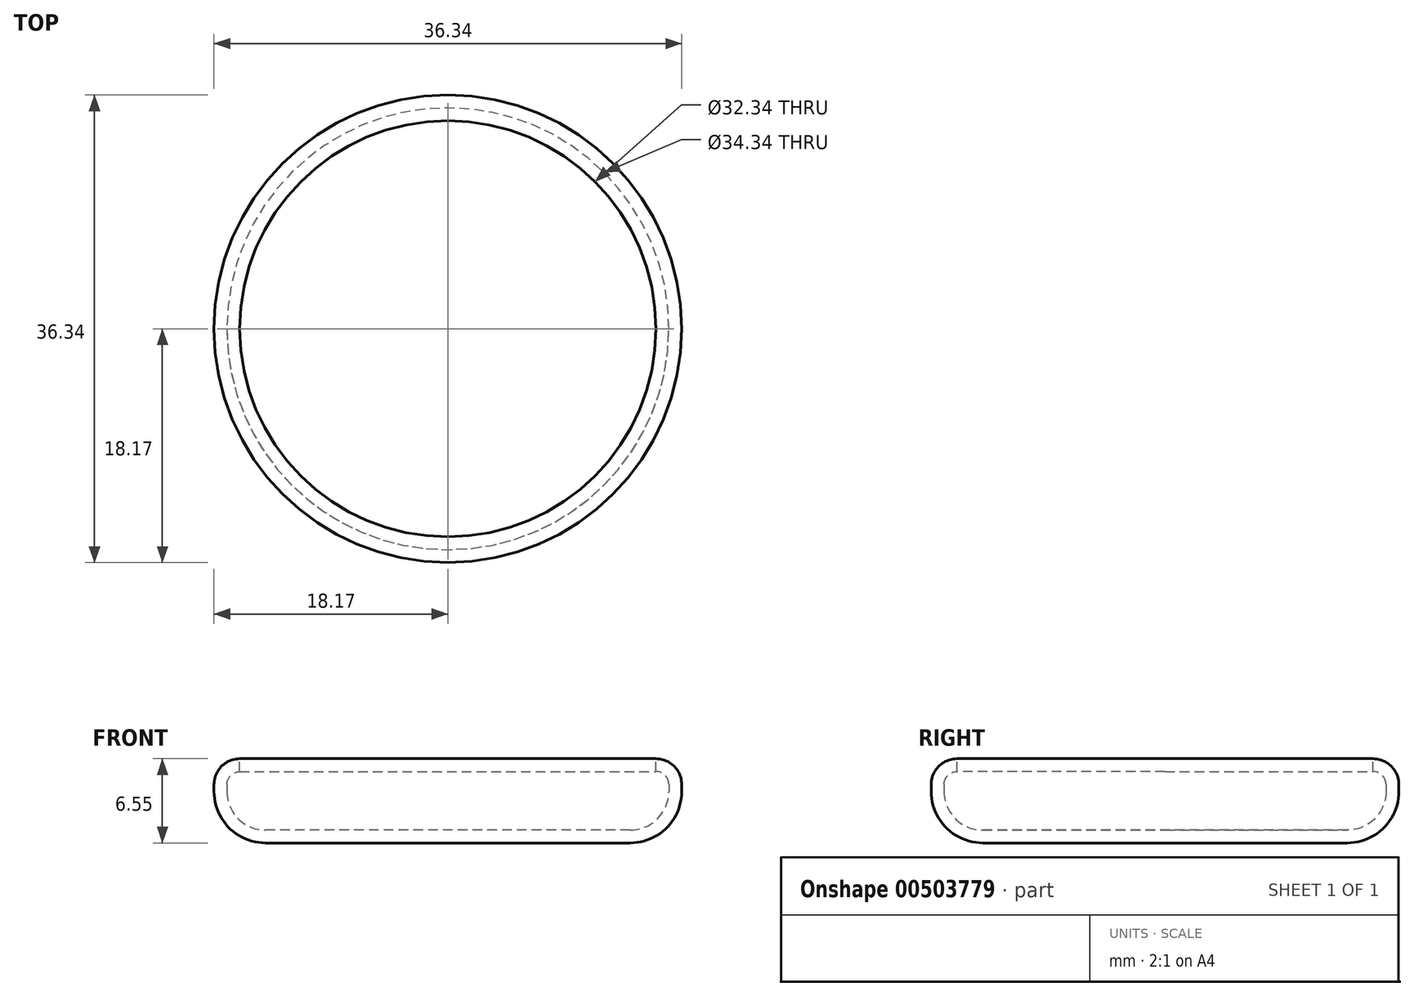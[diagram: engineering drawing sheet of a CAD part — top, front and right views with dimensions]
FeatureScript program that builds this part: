
annotation { "Feature Type Name" : "Feature", "Feature Type Description" : "" }
export const myFeature = defineFeature(function(context is Context, id is Id, definition is map)
    precondition{}
    {
        {
            var Q0;
            Q0=qCreatedBy(makeId("Top.planeOp"),FACE);
            var sketch = newSketch(context, id + "F0", { "sketchPlane" : qUnion([Q0])});
            skCircle(sketch, "E0", {"center": v(0, 0) * mm, "radius": 18.17 * mm});
            skSolve(sketch);
        }
        {
            var Q0;
            Q0=makeQuery(id+"F0.imprint","IMPRINT",FACE,{"disambiguationData":[TD([[makeQuery(id+"F0.imprint","IMPRINT",EDGE,{"derivedFrom":sQuery(id+"F0.wireOp",EDGE,"E0")}),1.0]])]});
            extrude(context, id + "F1", {"entities" : qUnion([Q0]), "depth" : 6.55 * mm});
        }
        {
            var Q0;
            Q0=makeQuery(id+"F1.opExtrude","CAP_EDGE",EDGE,{"disambiguationData":[OSD([sQuery(id+"F0.wireOp",EDGE,"E0")])],"isStart":true});
            fillet(context, id + "F2", {"entities" : qUnion([Q0]), "radius" : 4 * mm, "tangentPropagation" : true, "allowEdgeOverflow" : false});
        }
        {
            var Q0;
            Q0=makeQuery(id+"F1.opExtrude","CAP_EDGE",EDGE,{"disambiguationData":[OSD([sQuery(id+"F0.wireOp",EDGE,"E0")])],"isStart":false});
            fillet(context, id + "F3", {"entities" : qUnion([Q0]), "radius" : 2 * mm, "tangentPropagation" : true, "allowEdgeOverflow" : false});
        }
        {
            var Q0;
            Q0=makeQuery(id+"F1.opExtrude","CAP_FACE",FACE,{"disambiguationData":[OSD([sQuery(id+"F0.wireOp",EDGE,"E0")])],"isStart":false});
            shell(context, id + "F4", {"entities" : qUnion([Q0]), "thickness" : 1 * mm});
        }
        {
            var Q0;
            Q0=qCreatedBy(makeId("Top.planeOp"),FACE);
            cPlane(context, id + "F5", {"entities" : qUnion([Q0]), "cplaneType" : CPlaneType.OFFSET, "offset" : 3.22 * mm, "width" : 152.4 * mm, "height" : 152.4 * mm});
        }
    });
